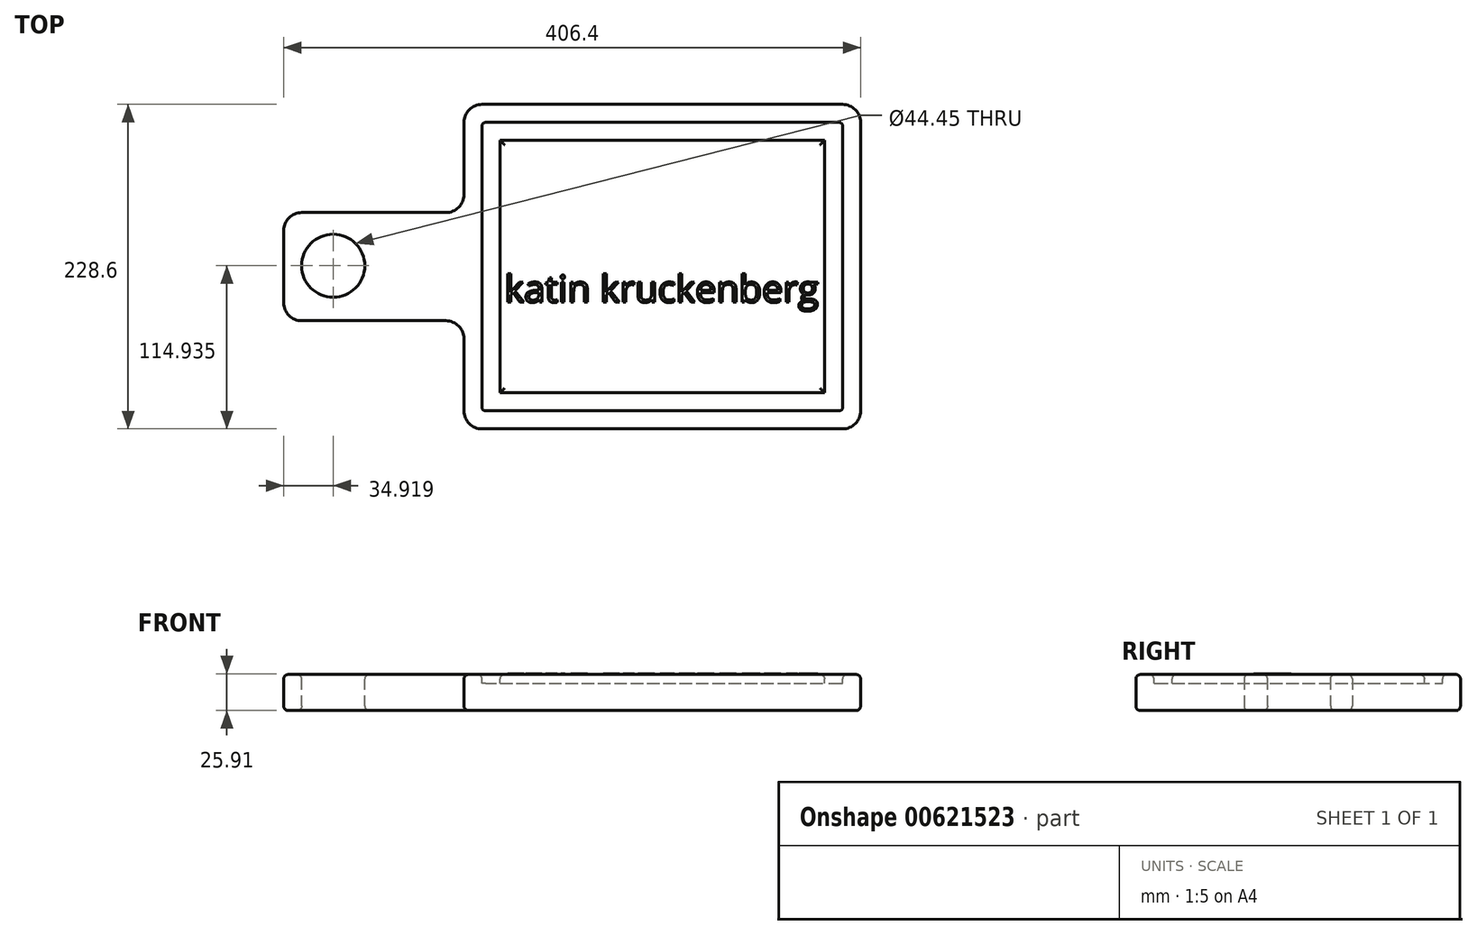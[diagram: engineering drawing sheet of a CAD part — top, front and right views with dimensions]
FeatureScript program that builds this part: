
annotation { "Feature Type Name" : "Feature", "Feature Type Description" : "" }
export const myFeature = defineFeature(function(context is Context, id is Id, definition is map)
    precondition{}
    {
        {
            var Q0;
            Q0=qCreatedBy(makeId("Top.planeOp"),FACE);
            var sketch = newSketch(context, id + "F0", { "sketchPlane" : qUnion([Q0])});
            skLineSegment(sketch, "E0.bottom", {"start": v(0, 0) * mm, "end": v(279.4, 0) * mm});
            skLineSegment(sketch, "E0.top", {"start": v(0, 228.6) * mm, "end": v(279.4, 228.6) * mm});
            skLineSegment(sketch, "E0.left", {"start": v(0, 0) * mm, "end": v(0, 228.6) * mm});
            skLineSegment(sketch, "E0.right", {"start": v(279.4, 0) * mm, "end": v(279.4, 228.6) * mm});
            skLineSegment(sketch, "E1.bottom", {"start": v(0, 152.4) * mm, "end": v(-127, 152.4) * mm});
            skLineSegment(sketch, "E1.top", {"start": v(0, 76.2) * mm, "end": v(-127, 76.2) * mm});
            skLineSegment(sketch, "E1.left", {"start": v(0, 152.4) * mm, "end": v(0, 76.2) * mm});
            skLineSegment(sketch, "E1.right", {"start": v(-127, 152.4) * mm, "end": v(-127, 76.2) * mm});
            skSolve(sketch);
        }
        {
            var Q0;
            {var subQ3=sQuery(id+"F0.wireOp",EDGE,"E0.bottom");Q0=makeQuery(id+"F0.imprint","IMPRINT",FACE,{"disambiguationData":[TD([[makeQuery(id+"F0.imprint","IMPRINT",EDGE,{"derivedFrom":subQ3}),1.0]])]});}
            var Q1;
            Q1=makeQuery(id+"F0.imprint","IMPRINT",FACE,{"disambiguationData":[TD([[makeQuery(id+"F0.imprint","IMPRINT",EDGE,{"derivedFrom":sQuery(id+"F0.wireOp",EDGE,"E1.bottom")}),1.0]])]});
            extrude(context, id + "F1", {"entities" : qUnion([Q0, Q1]), "depth" : 25.4 * mm, "offsetDistance" : 25.4 * mm});
        }
        {
            var Q0;
            Q0=makeQuery(id+"F1.opExtrude","CAP_FACE",FACE,{"disambiguationData":[OSD([sQuery(id+"F0.wireOp",EDGE,"E0.bottom"),sQuery(id+"F0.wireOp",EDGE,"E0.top"),sQuery(id+"F0.wireOp",EDGE,"E0.left"),sQuery(id+"F0.wireOp",EDGE,"E0.right"),sQuery(id+"F0.wireOp",EDGE,"E1.bottom"),sQuery(id+"F0.wireOp",EDGE,"E1.top"),sQuery(id+"F0.wireOp",EDGE,"E1.right")])],"isStart":false});
            var sketch = newSketch(context, id + "F2", { "sketchPlane" : qUnion([Q0])});
            skCircle(sketch, "E2", {"center": v(-92.08, 114.94) * mm, "radius": 22.23 * mm});
            skSolve(sketch);
        }
        {
            var Q0;
            Q0 = qSketchRegion(id + "F2", true);
            extrude(context, id + "F3", {"entities" : qUnion([Q0]), "operationType" : NewBodyOperationType.REMOVE, "oppositeDirection" : true, "depth" : 25.4 * mm, "offsetDistance" : 25.4 * mm});
        }
        {
            var Q0;
            Q0=makeQuery(id+"F1.opExtrude","CAP_FACE",FACE,{"disambiguationData":[OSD([sQuery(id+"F0.wireOp",EDGE,"E0.bottom"),sQuery(id+"F0.wireOp",EDGE,"E0.top"),sQuery(id+"F0.wireOp",EDGE,"E0.left"),sQuery(id+"F0.wireOp",EDGE,"E0.right"),sQuery(id+"F0.wireOp",EDGE,"E1.bottom"),sQuery(id+"F0.wireOp",EDGE,"E1.top"),sQuery(id+"F0.wireOp",EDGE,"E1.right")])],"isStart":false});
            var sketch = newSketch(context, id + "F4", { "sketchPlane" : qUnion([Q0])});
            skLineSegment(sketch, "E3.0", {"start": v(12.7, 215.9) * mm, "end": v(266.7, 215.9) * mm});
            skLineSegment(sketch, "E3.1", {"start": v(12.7, 12.7) * mm, "end": v(12.7, 215.9) * mm});
            skLineSegment(sketch, "E3.2", {"start": v(12.7, 12.7) * mm, "end": v(266.7, 12.7) * mm});
            skLineSegment(sketch, "E3.3", {"start": v(266.7, 12.7) * mm, "end": v(266.7, 215.9) * mm});
            skLineSegment(sketch, "E4.0", {"start": v(25.4, 203.2) * mm, "end": v(254, 203.2) * mm});
            skLineSegment(sketch, "E4.1", {"start": v(25.4, 25.4) * mm, "end": v(25.4, 203.2) * mm});
            skLineSegment(sketch, "E4.2", {"start": v(25.4, 25.4) * mm, "end": v(254, 25.4) * mm});
            skLineSegment(sketch, "E4.3", {"start": v(254, 25.4) * mm, "end": v(254, 203.2) * mm});
            skSolve(sketch);
        }
        {
            var Q0;
            Q0=makeQuery(id+"F4.imprint","IMPRINT",FACE,{"disambiguationData":[TD([[makeQuery(id+"F4.imprint","IMPRINT",EDGE,{"derivedFrom":sQuery(id+"F4.wireOp",EDGE,"E3.0")}),-1.0]])]});
            extrude(context, id + "F5", {"entities" : qUnion([Q0]), "operationType" : NewBodyOperationType.REMOVE, "oppositeDirection" : true, "depth" : 6.35 * mm, "offsetDistance" : 25.4 * mm});
        }
        {
            var Q0;
            Q0=makeQuery(id+"F5.boolean.opBoolean","COPY",EDGE,{"derivedFrom":makeQuery(id+"F5.opExtrude","SWEPT_EDGE",EDGE,{"disambiguationData":[OSD([sQuery(id+"F4.wireOp",EDGE,"E3.0"),sQuery(id+"F4.wireOp",EDGE,"E3.3")])]})});
            var Q1;
            Q1=makeQuery(id+"F5.boolean.opBoolean","COPY",EDGE,{"derivedFrom":makeQuery(id+"F5.opExtrude","SWEPT_EDGE",EDGE,{"disambiguationData":[OSD([sQuery(id+"F4.wireOp",EDGE,"E3.0"),sQuery(id+"F4.wireOp",EDGE,"E3.1")])]})});
            var Q2;
            Q2=makeQuery(id+"F5.boolean.opBoolean","COPY",EDGE,{"derivedFrom":makeQuery(id+"F5.opExtrude","SWEPT_EDGE",EDGE,{"disambiguationData":[OSD([sQuery(id+"F4.wireOp",EDGE,"E3.1"),sQuery(id+"F4.wireOp",EDGE,"E3.2")])]})});
            var Q3;
            Q3=makeQuery(id+"F5.boolean.opBoolean","COPY",EDGE,{"derivedFrom":makeQuery(id+"F5.opExtrude","SWEPT_EDGE",EDGE,{"disambiguationData":[OSD([sQuery(id+"F4.wireOp",EDGE,"E3.2"),sQuery(id+"F4.wireOp",EDGE,"E3.3")])]})});
            fillet(context, id + "F6", {"entities" : qUnion([Q0, Q1, Q2, Q3]), "radius" : 2.54 * mm, "tangentPropagation" : true, "allowEdgeOverflow" : false});
        }
        {
            var Q0;
            Q0=makeQuery(id+"F1.opExtrude","SWEPT_EDGE",EDGE,{"disambiguationData":[OSD([sQuery(id+"F0.wireOp",EDGE,"E0.bottom"),sQuery(id+"F0.wireOp",EDGE,"E0.left")])]});
            var Q1;
            Q1=makeQuery(id+"F1.opExtrude","SWEPT_EDGE",EDGE,{"disambiguationData":[OSD([sQuery(id+"F0.wireOp",EDGE,"E1.top"),sQuery(id+"F0.wireOp",EDGE,"E1.right")])]});
            var Q2;
            Q2=makeQuery(id+"F1.opExtrude","SWEPT_EDGE",EDGE,{"disambiguationData":[OSD([sQuery(id+"F0.wireOp",EDGE,"E0.bottom"),sQuery(id+"F0.wireOp",EDGE,"E0.right")])]});
            var Q3;
            Q3=makeQuery(id+"F1.opExtrude","SWEPT_EDGE",EDGE,{"disambiguationData":[OSD([sQuery(id+"F0.wireOp",EDGE,"E0.top"),sQuery(id+"F0.wireOp",EDGE,"E0.right")])]});
            var Q4;
            Q4=makeQuery(id+"F1.opExtrude","SWEPT_EDGE",EDGE,{"disambiguationData":[OSD([sQuery(id+"F0.wireOp",EDGE,"E0.top"),sQuery(id+"F0.wireOp",EDGE,"E0.left")])]});
            var Q5;
            Q5=makeQuery(id+"F1.opExtrude","SWEPT_EDGE",EDGE,{"disambiguationData":[OSD([sQuery(id+"F0.wireOp",EDGE,"E1.bottom"),sQuery(id+"F0.wireOp",EDGE,"E1.right")])]});
            var Q6;
            Q6=makeQuery(id+"F1.opExtrude","SWEPT_EDGE",EDGE,{"disambiguationData":[OSD([sQuery(id+"F0.wireOp",EDGE,"E0.left"),sQuery(id+"F0.wireOp",EDGE,"E1.bottom"),sQuery(id+"F0.wireOp",EDGE,"E1.left")])]});
            var Q7;
            Q7=makeQuery(id+"F1.opExtrude","SWEPT_EDGE",EDGE,{"disambiguationData":[OSD([sQuery(id+"F0.wireOp",EDGE,"E0.left"),sQuery(id+"F0.wireOp",EDGE,"E1.top"),sQuery(id+"F0.wireOp",EDGE,"E1.left")])]});
            fillet(context, id + "F7", {"entities" : qUnion([Q0, Q1, Q2, Q3, Q4, Q5, Q6, Q7]), "radius" : 12.7 * mm, "tangentPropagation" : true, "allowEdgeOverflow" : false});
        }
        {
            var Q0;
            {var subQ0=sQuery(id+"F0.wireOp",EDGE,"E0.top");var subQ1=sQuery(id+"F0.wireOp",EDGE,"E1.right");var subQ2=sQuery(id+"F0.wireOp",EDGE,"E1.top");var subQ3=sQuery(id+"F0.wireOp",EDGE,"E1.bottom");var subQ4=sQuery(id+"F0.wireOp",EDGE,"E0.right");var subQ5=sQuery(id+"F0.wireOp",EDGE,"E0.bottom");var subQ6=sQuery(id+"F0.wireOp",EDGE,"E0.left");Q0=makeQuery(id+"F5.boolean.opBoolean","SPLIT",FACE,{"disambiguationData":[TD([makeQuery(id+"F1.opExtrude","SWEPT_FACE",FACE,{"disambiguationData":[OSD([subQ5])]})])],"derivedFrom":makeQuery(id+"F1.opExtrude","CAP_FACE",FACE,{"disambiguationData":[OSD([subQ5,subQ0,subQ6,subQ4,subQ3,subQ2,subQ1])],"isStart":false})});}
            var Q1;
            Q1=makeQuery(id+"F5.boolean.opBoolean","SPLIT",FACE,{"disambiguationData":[TD([makeQuery(id+"F5.opExtrude","SWEPT_FACE",FACE,{"disambiguationData":[OSD([sQuery(id+"F4.wireOp",EDGE,"E4.0")])]})])],"derivedFrom":makeQuery(id+"F1.opExtrude","CAP_FACE",FACE,{"disambiguationData":[OSD([sQuery(id+"F0.wireOp",EDGE,"E0.bottom"),sQuery(id+"F0.wireOp",EDGE,"E0.top"),sQuery(id+"F0.wireOp",EDGE,"E0.left"),sQuery(id+"F0.wireOp",EDGE,"E0.right"),sQuery(id+"F0.wireOp",EDGE,"E1.bottom"),sQuery(id+"F0.wireOp",EDGE,"E1.top"),sQuery(id+"F0.wireOp",EDGE,"E1.right")])],"isStart":false})});
            var Q2;
            Q2=makeQuery(id+"F1.opExtrude","CAP_FACE",FACE,{"disambiguationData":[OSD([sQuery(id+"F0.wireOp",EDGE,"E0.bottom"),sQuery(id+"F0.wireOp",EDGE,"E0.top"),sQuery(id+"F0.wireOp",EDGE,"E0.left"),sQuery(id+"F0.wireOp",EDGE,"E0.right"),sQuery(id+"F0.wireOp",EDGE,"E1.bottom"),sQuery(id+"F0.wireOp",EDGE,"E1.top"),sQuery(id+"F0.wireOp",EDGE,"E1.right")])],"isStart":true});
            fillet(context, id + "F8", {"entities" : qUnion([Q0, Q1, Q2]), "radius" : 3.17 * mm, "tangentPropagation" : true, "allowEdgeOverflow" : false});
        }
        {
            var Q0;
            Q0=makeQuery(id+"F5.boolean.opBoolean","SPLIT",FACE,{"disambiguationData":[TD([makeQuery(id+"F5.opExtrude","SWEPT_FACE",FACE,{"disambiguationData":[OSD([sQuery(id+"F4.wireOp",EDGE,"E4.0")])]})])],"derivedFrom":makeQuery(id+"F1.opExtrude","CAP_FACE",FACE,{"disambiguationData":[OSD([sQuery(id+"F0.wireOp",EDGE,"E0.bottom"),sQuery(id+"F0.wireOp",EDGE,"E0.top"),sQuery(id+"F0.wireOp",EDGE,"E0.left"),sQuery(id+"F0.wireOp",EDGE,"E0.right"),sQuery(id+"F0.wireOp",EDGE,"E1.bottom"),sQuery(id+"F0.wireOp",EDGE,"E1.top"),sQuery(id+"F0.wireOp",EDGE,"E1.right")])],"isStart":false})});
            var sketch = newSketch(context, id + "F9", { "sketchPlane" : qUnion([Q0])});
            skText(sketch, "E5", { "text": "katin kruckenberg", "fontName": "OpenSans-Regular.ttf"});
            const initialGuessF9  = {"E5": [0.02858, 0.08923, 1, 0, 0.01893]};
            skSetInitialGuess(sketch, initialGuessF9);
            skSolve(sketch);
        }
        {
            var Q0;
            Q0 = qSketchRegion(id + "F9", true);
            extrude(context, id + "F10", {"entities" : qUnion([Q0]), "operationType" : NewBodyOperationType.ADD, "depth" : 0.5 * mm, "offsetDistance" : 25.4 * mm});
        }
    });
